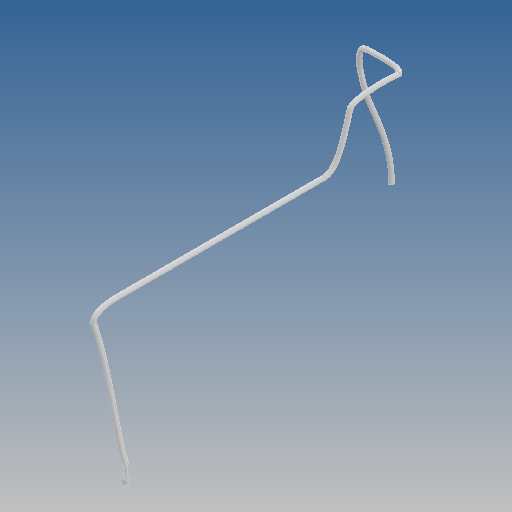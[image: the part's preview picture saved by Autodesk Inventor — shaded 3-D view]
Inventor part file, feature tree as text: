
AUTODESK INVENTOR PART (.ipt)
format: ipt  version: 2020 (Build 240168000, 168)  size: 535,552 bytes
history: native  units: mm
features: sketch x17, sweep x7, reference x3, extrude x2, projected_geometry x2, other x2, revolve x1, chamfer x1, pattern_circular x1
ambient origin geometry x8: Origin, YZ Plane, XZ Plane, XY Plane, X Axis, Y Axis, Z Axis, Center Point
bodies: Solid1 (feature_tree)
feature tree (36):
  revolve  "Revolution1"  [1 undecoded]
  extrude  "Extrusion1"  Depth=2.15mm
  extrude  "Extrusion2"  Depth=20.0mm
  chamfer  "Chamfer1"  Distance=9.0mm
  pattern_circular  "Circular Pattern1"  Count=4 Angle=360.0deg
  sweep  "Sweep2"
  sweep  "Sweep3"
  sweep  "Sweep4"
  sweep  "Sweep5"
  sweep  "Sweep6"
  sweep  "Sweep7"
  sweep  "Sweep8"
  sketch  "Sketch1"  dims[d0=5.4mm d1=1.5mm]
  sketch  "Sketch2"  dims[d2=7.53mm d3=2.15mm]
  sketch  "Sketch3"  dims[d4=1.5mm d5=20.0mm]
  sketch  "Sketch4"  dims[d6=90.0deg]
  sketch  "Sketch5"  dims[d7=4.0mm d8=9.0mm d9=0.0mm]
  sketch  "Sketch6"  dims[d10=1.11mm]
  sketch  "Sketch7"  dims[d11=8.35mm]
  projected_geometry  "Projected Loop1"
  sketch  "Sketch9"  dims[d12=1.594218mm]
  projected_geometry  "Projected Loop2"
  sketch  "Sketch10"  dims[d13=6.7mm d14=0.0mm]
  sketch  "Sketch11"  dims[d15=0.5mm d16=2.0mm d17=45.0deg d18=40.0mm d19=360.0deg]
  sketch  "Sketch12"  dims[d21=8.0mm d24=0.0mm d25=0.0mm]
  sketch  "Sketch14"  dims[d26=0.0mm d27=0.0mm d28=0.0mm d29=0.0mm]
  reference  "Reference2"
  sketch  "Sketch15"  dims[d30=0.0mm d31=0.0mm d32=0.0mm d33=0.0mm]
  sketch  "Sketch19"  dims[d34=0.0mm d35=0.0mm d36=0.0mm d37=0.0mm]
  sketch  "Sketch20"
  reference  "Reference7"
  sketch  "Sketch21"
  sketch  "Sketch22"
  reference  "Reference9"
  other  "30-00 Injectomat suplimentar.iam"
  other  "0008-30-1008 Adaptor furtun:1"
note: 1 required parameter value undecoded (feature->parameter linkage not recoverable at this tier; creation-order binding heuristic only, values carry confidence <= 0.55)
